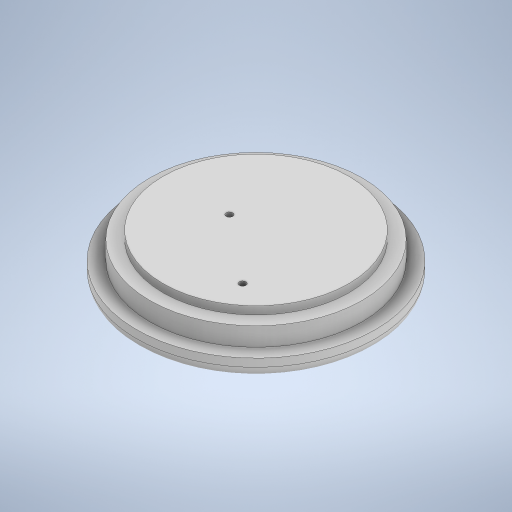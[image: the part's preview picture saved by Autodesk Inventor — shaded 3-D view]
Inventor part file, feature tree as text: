
AUTODESK INVENTOR PART (.ipt)
format: ipt  version: 2024 (Build 280153000, 153)  size: 276,992 bytes
history: native  units: mm
features: extrude x4, sketch x3, fillet x1
ambient origin geometry x8: Origin, YZ Plane, XZ Plane, XY Plane, X Axis, Y Axis, Z Axis, Center Point
bodies: Solid1 (feature_tree)
feature tree (8):
  sketch  "Sketch1"  dims[d0=80.0mm d1=70.0mm]
  extrude  "Extrusion1"  Depth=70.0mm
  extrude  "Extrusion2"  Depth=7.0mm TaperAngle=0.0deg
  extrude  "Extrusion4"  Depth=7.0mm TaperAngle=0.0deg
  fillet  "Fillet1"  Radius=4.0mm
  extrude  "Extrusion5"  Depth=5.0mm
  sketch  "Sketch3"  dims[d2=10.0mm d3=0.0mm d4=7.0mm d5=0.0mm]
  sketch  "Sketch4"  dims[d14=90.0mm d15=7.0mm d16=0.0mm d17=4.0mm d24=24.0mm d25=54.0mm d26=10.0mm d27=2.5mm d28=2.5mm d29=5.0mm d30=0.0mm d31=25.0mm]
